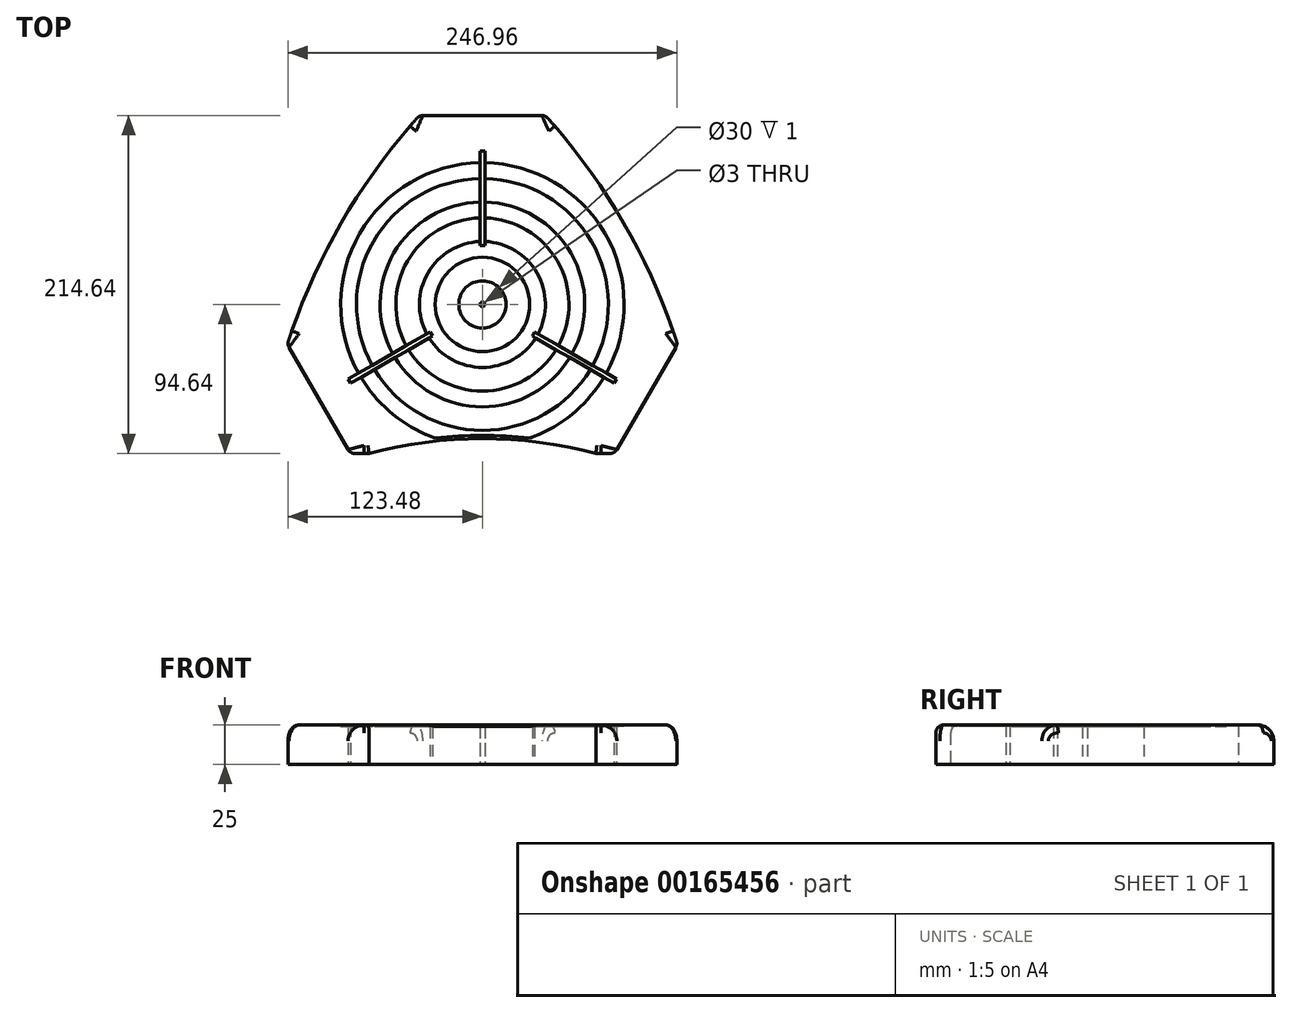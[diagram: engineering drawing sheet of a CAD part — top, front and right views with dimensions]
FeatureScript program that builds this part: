
annotation { "Feature Type Name" : "Feature", "Feature Type Description" : "" }
export const myFeature = defineFeature(function(context is Context, id is Id, definition is map)
    precondition{}
    {
        {
            var Q0;
            Q0=qCreatedBy(makeId("Top.planeOp"),FACE);
            var sketch = newSketch(context, id + "F0", { "sketchPlane" : qUnion([Q0])});
            skLineSegment(sketch, "E0", {"start": v(0, 0) * mm, "end": v(0, 120) * mm});
            skLineSegment(sketch, "E1", {"start": v(0, 0) * mm, "end": v(-82.55, 47.66) * mm, "construction": true});
            skLineSegment(sketch, "E2.MirrorCS", {"start": v(0, 0) * mm, "end": v(-103.92, -60) * mm, "construction": true});
            skLineSegment(sketch, "E3.MirrorCS", {"start": v(0, 0) * mm, "end": v(103.92, -60) * mm, "construction": true});
            skLineSegment(sketch, "E4", {"start": v(0, 120) * mm, "end": v(-40, 120) * mm});
            skLineSegment(sketch, "E5.MirrorCS", {"start": v(0, 120) * mm, "end": v(40, 120) * mm});
            skLineSegment(sketch, "E6", {"start": v(-103.92, -60) * mm, "end": v(-123.92, -25.36) * mm});
            skLineSegment(sketch, "E7", {"start": v(103.92, -60) * mm, "end": v(83.92, -94.64) * mm});
            skLineSegment(sketch, "E8.MirrorCS", {"start": v(103.92, -60) * mm, "end": v(123.92, -25.36) * mm});
            skLineSegment(sketch, "E9.MirrorCS", {"start": v(0, 0) * mm, "end": v(0, 120) * mm, "construction": true});
            skLineSegment(sketch, "E10.MirrorCS", {"start": v(-103.92, -60) * mm, "end": v(-83.92, -94.64) * mm});
            skLineSegment(sketch, "E11", {"start": v(-40, 120) * mm, "end": v(-123.92, -25.36) * mm, "construction": true});
            skLineSegment(sketch, "E12", {"start": v(40, 120) * mm, "end": v(123.92, -25.36) * mm, "construction": true});
            skLineSegment(sketch, "E13", {"start": v(-83.92, -94.64) * mm, "end": v(83.92, -94.64) * mm, "construction": true});
            skArc(sketch, "E14", {"start": v(-40, 120) * mm, "mid": v(-89.67, 51.77) * mm, "end": v(-123.92, -25.36) * mm});
            skArc(sketch, "E15.MirrorCS", {"start": v(40, 120) * mm, "mid": v(89.67, 51.77) * mm, "end": v(123.92, -25.36) * mm});
            skLineSegment(sketch, "E16", {"start": v(-72.04, -85.4) * mm, "end": v(-72.04, -103.36) * mm, "construction": true});
            skLineSegment(sketch, "E17.MirrorCS", {"start": v(72.04, -85.4) * mm, "end": v(72.04, -103.36) * mm, "construction": true});
            skArc(sketch, "E18", {"start": v(72.04, -94.64) * mm, "mid": v(0, -85.21) * mm, "end": v(-72.04, -94.64) * mm});
            skLineSegment(sketch, "E19", {"start": v(-72.04, -94.64) * mm, "end": v(-83.92, -94.64) * mm});
            skLineSegment(sketch, "E20", {"start": v(72.04, -94.64) * mm, "end": v(83.92, -94.64) * mm});
            skLineSegment(sketch, "E21.bottom", {"start": v(1.5, 97.5) * mm, "end": v(-1.5, 97.5) * mm});
            skLineSegment(sketch, "E21.top", {"start": v(1.5, 37.5) * mm, "end": v(-1.5, 37.5) * mm});
            skLineSegment(sketch, "E21.left", {"start": v(1.5, 97.5) * mm, "end": v(1.5, 37.5) * mm});
            skLineSegment(sketch, "E21.right", {"start": v(-1.5, 97.5) * mm, "end": v(-1.5, 37.5) * mm});
            skPoint(sketch, "E21.middle", {"position": v(0, 67.5) * mm});
            skLineSegment(sketch, "E22.MirrorCS", {"start": v(-31.73, -20.05) * mm, "end": v(-33.23, -17.45) * mm});
            skLineSegment(sketch, "E23.MirrorCS", {"start": v(-83.69, -50.05) * mm, "end": v(-85.19, -47.45) * mm});
            skLineSegment(sketch, "E24.MirrorCS", {"start": v(-85.19, -47.45) * mm, "end": v(-33.23, -17.45) * mm});
            skLineSegment(sketch, "E25.MirrorCS", {"start": v(-83.69, -50.05) * mm, "end": v(-31.73, -20.05) * mm});
            skPoint(sketch, "E26.MirrorP", {"position": v(-58.46, -33.75) * mm});
            skLineSegment(sketch, "E27.MirrorCS", {"start": v(31.73, -20.05) * mm, "end": v(33.23, -17.45) * mm});
            skLineSegment(sketch, "E28.MirrorCS", {"start": v(83.69, -50.05) * mm, "end": v(85.19, -47.45) * mm});
            skLineSegment(sketch, "E29.MirrorCS", {"start": v(85.19, -47.45) * mm, "end": v(33.23, -17.45) * mm});
            skLineSegment(sketch, "E30.MirrorCS", {"start": v(83.69, -50.05) * mm, "end": v(31.73, -20.05) * mm});
            skPoint(sketch, "E31.MirrorP", {"position": v(58.46, -33.75) * mm});
            skSolve(sketch);
        }
        {
            var Q0;
            Q0 = qSketchRegion(id + "F0", true);
            extrude(context, id + "F1", {"entities" : qUnion([Q0]), "depth" : 25 * mm});
        }
        {
            var Q0;
            Q0=makeQuery(id+"F1.opExtrude","CAP_EDGE",EDGE,{"disambiguationData":[OSD([sQuery(id+"F0.wireOp",EDGE,"E5.MirrorCS"),sQuery(id+"F0.wireOp",EDGE,"E4")])],"isStart":false});
            var Q1;
            Q1=makeQuery(id+"F1.opExtrude","CAP_EDGE",EDGE,{"disambiguationData":[OSD([sQuery(id+"F0.wireOp",EDGE,"E6"),sQuery(id+"F0.wireOp",EDGE,"E10.MirrorCS")])],"isStart":false});
            var Q2;
            Q2=makeQuery(id+"F1.opExtrude","CAP_EDGE",EDGE,{"disambiguationData":[OSD([sQuery(id+"F0.wireOp",EDGE,"E7"),sQuery(id+"F0.wireOp",EDGE,"E8.MirrorCS")])],"isStart":false});
            fillet(context, id + "F2", {"entities" : qUnion([Q0, Q1, Q2]), "radius" : 10 * mm, "tangentPropagation" : true, "allowEdgeOverflow" : false});
        }
        {
            var Q0;
            Q0=makeQuery(id+"F1.opExtrude","SWEPT_EDGE",EDGE,{"disambiguationData":[OSD([sQuery(id+"F0.wireOp",EDGE,"E8.MirrorCS"),sQuery(id+"F0.wireOp",EDGE,"E15.MirrorCS")])]});
            var Q1;
            Q1=makeQuery(id+"F1.opExtrude","SWEPT_EDGE",EDGE,{"disambiguationData":[OSD([sQuery(id+"F0.wireOp",EDGE,"E4"),sQuery(id+"F0.wireOp",EDGE,"E14")])]});
            var Q2;
            Q2=makeQuery(id+"F1.opExtrude","SWEPT_EDGE",EDGE,{"disambiguationData":[OSD([sQuery(id+"F0.wireOp",EDGE,"E10.MirrorCS"),sQuery(id+"F0.wireOp",EDGE,"E19")])]});
            var Q3;
            Q3=makeQuery(id+"F1.opExtrude","SWEPT_EDGE",EDGE,{"disambiguationData":[OSD([sQuery(id+"F0.wireOp",EDGE,"E7"),sQuery(id+"F0.wireOp",EDGE,"E20")])]});
            var Q4;
            Q4=makeQuery(id+"F1.opExtrude","CAP_EDGE",EDGE,{"disambiguationData":[OSD([sQuery(id+"F0.wireOp",EDGE,"E18")])],"isStart":false});
            fillet(context, id + "F3", {"entities" : qUnion([Q0, Q1, Q2, Q3, Q4]), "radius" : 5 * mm, "tangentPropagation" : true, "allowEdgeOverflow" : false});
        }
        {
            var Q0;
            Q0=makeQuery(id+"F1.opExtrude","CAP_FACE",FACE,{"disambiguationData":[OSD([sQuery(id+"F0.wireOp",EDGE,"E5.MirrorCS"),sQuery(id+"F0.wireOp",EDGE,"E6"),sQuery(id+"F0.wireOp",EDGE,"E7"),sQuery(id+"F0.wireOp",EDGE,"E8.MirrorCS"),sQuery(id+"F0.wireOp",EDGE,"E4"),sQuery(id+"F0.wireOp",EDGE,"E10.MirrorCS"),sQuery(id+"F0.wireOp",EDGE,"E14"),sQuery(id+"F0.wireOp",EDGE,"E15.MirrorCS"),sQuery(id+"F0.wireOp",EDGE,"E18"),sQuery(id+"F0.wireOp",EDGE,"E19"),sQuery(id+"F0.wireOp",EDGE,"E20"),sQuery(id+"F0.wireOp",EDGE,"E21.bottom"),sQuery(id+"F0.wireOp",EDGE,"E21.left"),sQuery(id+"F0.wireOp",EDGE,"E22.MirrorCS"),sQuery(id+"F0.wireOp",EDGE,"E23.MirrorCS"),sQuery(id+"F0.wireOp",EDGE,"E24.MirrorCS"),sQuery(id+"F0.wireOp",EDGE,"E25.MirrorCS"),sQuery(id+"F0.wireOp",EDGE,"E21.top"),sQuery(id+"F0.wireOp",EDGE,"E21.right"),sQuery(id+"F0.wireOp",EDGE,"E27.MirrorCS"),sQuery(id+"F0.wireOp",EDGE,"E28.MirrorCS"),sQuery(id+"F0.wireOp",EDGE,"E29.MirrorCS"),sQuery(id+"F0.wireOp",EDGE,"E30.MirrorCS")])],"isStart":false});
            var sketch = newSketch(context, id + "F4", { "sketchPlane" : qUnion([Q0])});
            skCircle(sketch, "E32", {"center": v(0, 0) * mm, "radius": 15 * mm});
            skCircle(sketch, "E33", {"center": v(0, 0) * mm, "radius": 30 * mm});
            skCircle(sketch, "E34", {"center": v(0, 0) * mm, "radius": 40 * mm});
            skCircle(sketch, "E35", {"center": v(0, 0) * mm, "radius": 55 * mm});
            skCircle(sketch, "E36", {"center": v(0, 0) * mm, "radius": 65 * mm});
            skCircle(sketch, "E37", {"center": v(0, 0) * mm, "radius": 80 * mm});
            skCircle(sketch, "E38", {"center": v(0, 0) * mm, "radius": 90 * mm});
            skSolve(sketch);
        }
        {
            var Q0;
            Q0 = qSketchRegion(id + "F4", true);
            var Q1;
            Q1=makeQuery(id+"F4.imprint","IMPRINT",FACE,{"disambiguationData":[TD([[makeQuery(id+"F4.imprint","IMPRINT",EDGE,{"derivedFrom":sQuery(id+"F4.wireOp",EDGE,"E32")}),1.0]])]});
            var Q2;
            Q2=makeQuery(id+"F4.imprint","IMPRINT",FACE,{"disambiguationData":[TD([[makeQuery(id+"F4.imprint","IMPRINT",EDGE,{"derivedFrom":sQuery(id+"F4.wireOp",EDGE,"E33")}),-1.0]])]});
            var Q3;
            {var subQ0=sQuery(id+"F4.wireOp",EDGE,"E35");var subQ1=makeQuery(id+"F1.opExtrude","CAP_EDGE",EDGE,{"disambiguationData":[OSD([sQuery(id+"F0.wireOp",EDGE,"E21.right")])],"isStart":false});var subQ2=makeQuery(id+"F4.imprint","INTERSECT",VERTEX,{"derivedFrom":[subQ1,subQ0]});Q3=makeQuery(id+"F4.imprint","IMPRINT",FACE,{"disambiguationData":[TD([[makeQuery(id+"F4.imprint","IMPRINT",EDGE,{"disambiguationData":[TD([[subQ2,-1.0]])],"derivedFrom":subQ0}),-1.0]])]});}
            var Q4;
            {var subQ0=sQuery(id+"F4.wireOp",EDGE,"E35");var subQ1=makeQuery(id+"F1.opExtrude","CAP_EDGE",EDGE,{"disambiguationData":[OSD([sQuery(id+"F0.wireOp",EDGE,"E21.left")])],"isStart":false});var subQ2=makeQuery(id+"F4.imprint","INTERSECT",VERTEX,{"derivedFrom":[subQ1,subQ0]});Q4=makeQuery(id+"F4.imprint","IMPRINT",FACE,{"disambiguationData":[TD([[makeQuery(id+"F4.imprint","IMPRINT",EDGE,{"disambiguationData":[TD([[subQ2,1.0]])],"derivedFrom":subQ0}),-1.0]])]});}
            var Q5;
            {var subQ0=sQuery(id+"F4.wireOp",EDGE,"E35");var subQ1=makeQuery(id+"F1.opExtrude","CAP_EDGE",EDGE,{"disambiguationData":[OSD([sQuery(id+"F0.wireOp",EDGE,"E25.MirrorCS")])],"isStart":false});var subQ2=makeQuery(id+"F4.imprint","INTERSECT",VERTEX,{"derivedFrom":[subQ1,subQ0]});Q5=makeQuery(id+"F4.imprint","IMPRINT",FACE,{"disambiguationData":[TD([[makeQuery(id+"F4.imprint","IMPRINT",EDGE,{"disambiguationData":[TD([[subQ2,-1.0]])],"derivedFrom":subQ0}),-1.0]])]});}
            extrude(context, id + "F5", {"entities" : qUnion([Q0, Q1, Q2, Q3, Q4, Q5]), "operationType" : NewBodyOperationType.REMOVE, "oppositeDirection" : true, "depth" : 1 * mm});
        }
        {
            var Q0;
            Q0=makeQuery(id+"F1.opExtrude","CAP_FACE",FACE,{"disambiguationData":[OSD([sQuery(id+"F0.wireOp",EDGE,"E5.MirrorCS"),sQuery(id+"F0.wireOp",EDGE,"E6"),sQuery(id+"F0.wireOp",EDGE,"E7"),sQuery(id+"F0.wireOp",EDGE,"E8.MirrorCS"),sQuery(id+"F0.wireOp",EDGE,"E4"),sQuery(id+"F0.wireOp",EDGE,"E10.MirrorCS"),sQuery(id+"F0.wireOp",EDGE,"E14"),sQuery(id+"F0.wireOp",EDGE,"E15.MirrorCS"),sQuery(id+"F0.wireOp",EDGE,"E18"),sQuery(id+"F0.wireOp",EDGE,"E19"),sQuery(id+"F0.wireOp",EDGE,"E20"),sQuery(id+"F0.wireOp",EDGE,"E21.bottom"),sQuery(id+"F0.wireOp",EDGE,"E21.left"),sQuery(id+"F0.wireOp",EDGE,"E22.MirrorCS"),sQuery(id+"F0.wireOp",EDGE,"E23.MirrorCS"),sQuery(id+"F0.wireOp",EDGE,"E24.MirrorCS"),sQuery(id+"F0.wireOp",EDGE,"E25.MirrorCS"),sQuery(id+"F0.wireOp",EDGE,"E21.top"),sQuery(id+"F0.wireOp",EDGE,"E21.right"),sQuery(id+"F0.wireOp",EDGE,"E27.MirrorCS"),sQuery(id+"F0.wireOp",EDGE,"E28.MirrorCS"),sQuery(id+"F0.wireOp",EDGE,"E29.MirrorCS"),sQuery(id+"F0.wireOp",EDGE,"E30.MirrorCS")])],"isStart":true});
            var sketch = newSketch(context, id + "F6", { "sketchPlane" : qUnion([Q0])});
            skCircle(sketch, "E39", {"center": v(0, 0) * mm, "radius": 1.5 * mm});
            skSolve(sketch);
        }
        {
            var Q0;
            Q0 = qSketchRegion(id + "F6", true);
            extrude(context, id + "F7", {"entities" : qUnion([Q0]), "operationType" : NewBodyOperationType.REMOVE, "endBound" : BoundingType.UP_TO_NEXT, "oppositeDirection" : true, "depth" : 25 * mm});
        }
    });
